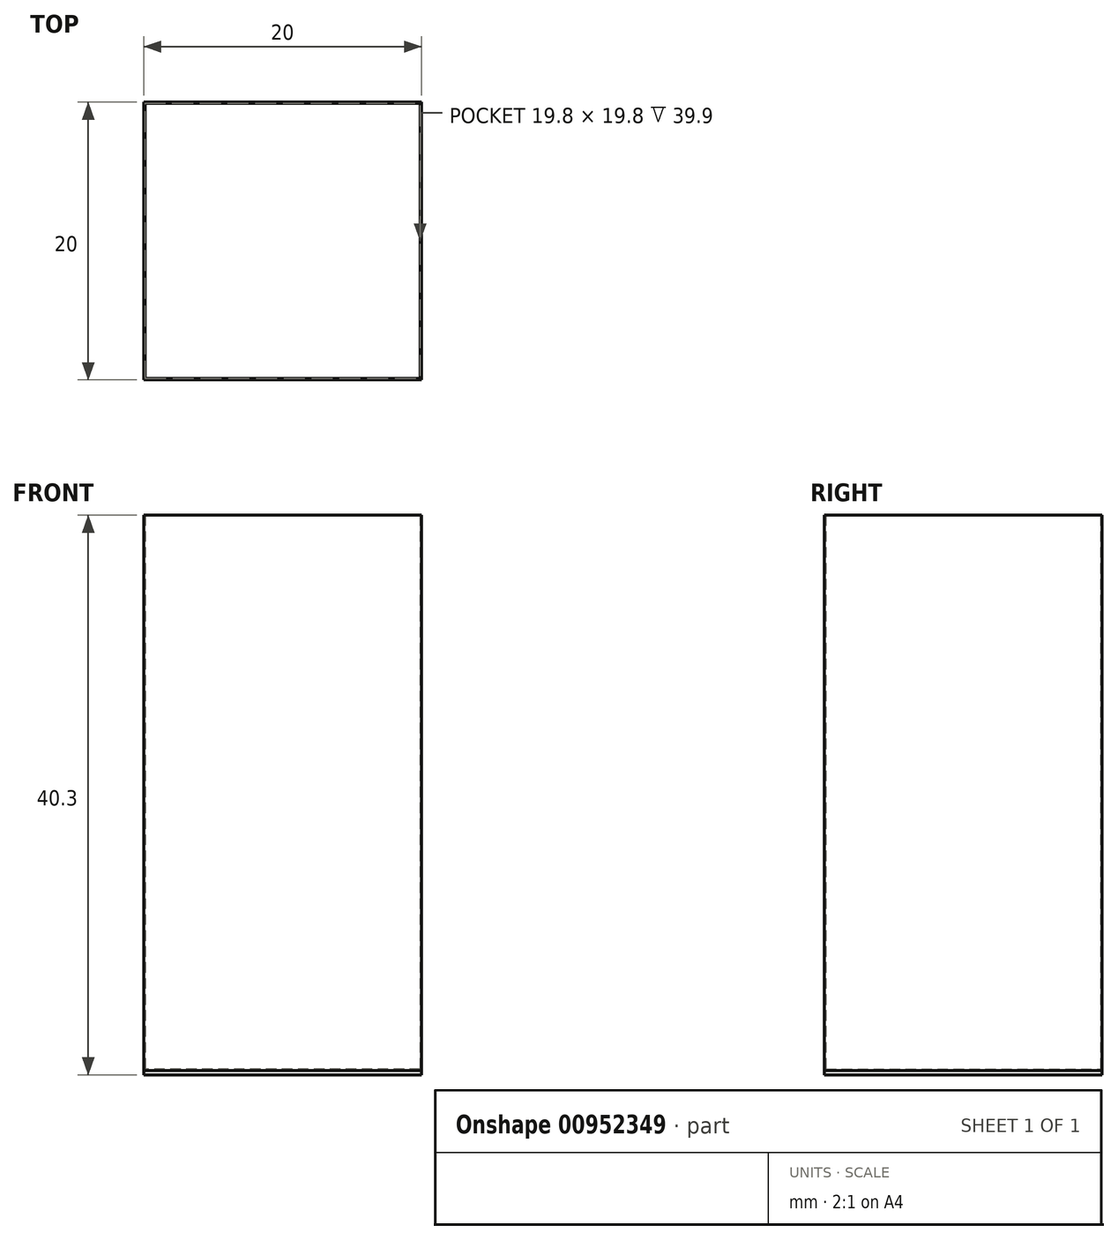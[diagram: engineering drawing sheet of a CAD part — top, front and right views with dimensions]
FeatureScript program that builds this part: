
annotation { "Feature Type Name" : "Feature", "Feature Type Description" : "" }
export const myFeature = defineFeature(function(context is Context, id is Id, definition is map)
    precondition{}
    {
        {
            var Q0;
            Q0=qCreatedBy(makeId("Top.planeOp"),FACE);
            var sketch = newSketch(context, id + "F0", { "sketchPlane" : qUnion([Q0])});
            skLineSegment(sketch, "E0.bottom", {"start": v(10, -10) * mm, "end": v(-10, -10) * mm});
            skLineSegment(sketch, "E0.top", {"start": v(10, 10) * mm, "end": v(-10, 10) * mm});
            skLineSegment(sketch, "E0.left", {"start": v(10, -10) * mm, "end": v(10, 10) * mm});
            skLineSegment(sketch, "E0.right", {"start": v(-10, -10) * mm, "end": v(-10, 10) * mm});
            skPoint(sketch, "E0.middle", {"position": v(0, 0) * mm});
            skSolve(sketch);
        }
        {
            var Q0;
            Q0=makeQuery(id+"F0.imprint","IMPRINT",FACE,{"disambiguationData":[TD([[makeQuery(id+"F0.imprint","IMPRINT",EDGE,{"derivedFrom":sQuery(id+"F0.wireOp",EDGE,"E0.bottom")}),-1.0]])]});
            extrude(context, id + "F1", {"entities" : qUnion([Q0]), "depth" : 0.3 * mm, "offsetDistance" : 25 * mm});
        }
        {
            var Q0;
            Q0=makeQuery(id+"F1.opExtrude","CAP_FACE",FACE,{"disambiguationData":[OSD([sQuery(id+"F0.wireOp",EDGE,"E0.bottom"),sQuery(id+"F0.wireOp",EDGE,"E0.top"),sQuery(id+"F0.wireOp",EDGE,"E0.left"),sQuery(id+"F0.wireOp",EDGE,"E0.right")])],"isStart":false});
            extrude(context, id + "F2", {"entities" : qUnion([Q0]), "depth" : 40 * mm, "offsetDistance" : 25 * mm});
        }
        {
            var Q0;
            Q0=makeQuery(id+"F2.opExtrude","CAP_FACE",FACE,{"disambiguationData":[OSD([sQuery(id+"F0.wireOp",EDGE,"E0.bottom"),sQuery(id+"F0.wireOp",EDGE,"E0.top"),sQuery(id+"F0.wireOp",EDGE,"E0.left"),sQuery(id+"F0.wireOp",EDGE,"E0.right")])],"isStart":false});
            shell(context, id + "F3", {"entities" : qUnion([Q0]), "thickness" : 0.1 * mm});
        }
    });
